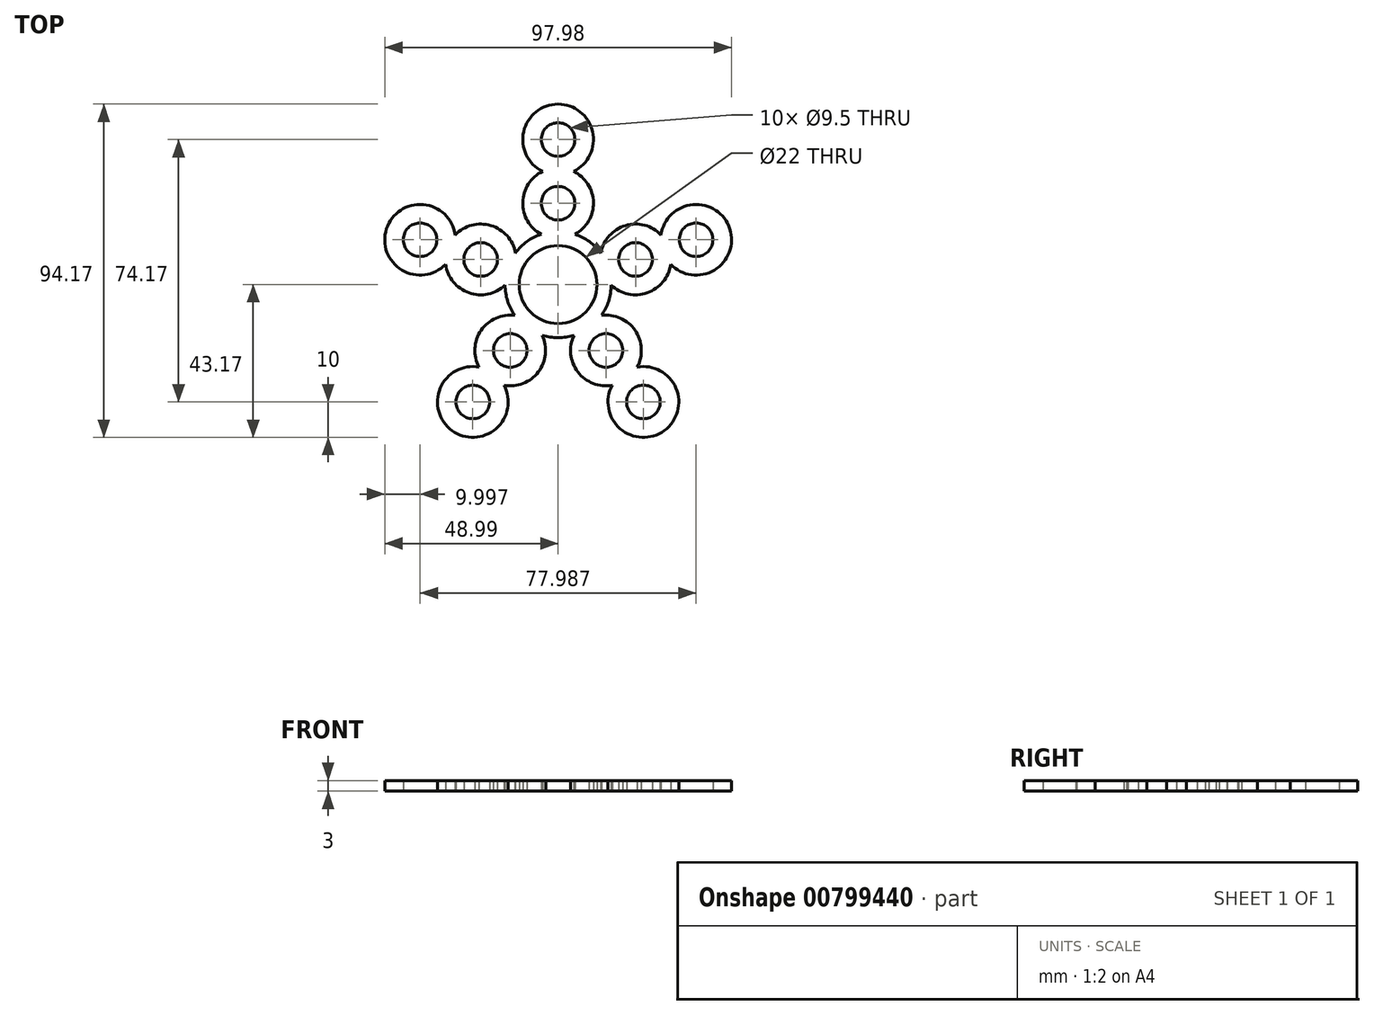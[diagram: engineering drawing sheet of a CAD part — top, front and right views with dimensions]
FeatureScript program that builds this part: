
annotation { "Feature Type Name" : "Feature", "Feature Type Description" : "" }
export const myFeature = defineFeature(function(context is Context, id is Id, definition is map)
    precondition{}
    {
        {
            var Q0;
            Q0=qCreatedBy(makeId("Top.planeOp"),FACE);
            var sketch = newSketch(context, id + "F0", { "sketchPlane" : qUnion([Q0])});
            skCircle(sketch, "E0", {"center": v(0, 0) * mm, "radius": 11 * mm});
            skArc(sketch, "E1", {"start": v(-4.78, 14.22) * mm, "mid": v(-8.82, 12.14) * mm, "end": v(-12.04, 8.94) * mm});
            skLineSegment(sketch, "E2", {"start": v(0, 0) * mm, "end": v(0, 23) * mm});
            skCircle(sketch, "E3", {"center": v(0, 23) * mm, "radius": 4.75 * mm});
            skArc(sketch, "E4", {"start": v(-4.36, 32) * mm, "mid": v(-10, 23.24) * mm, "end": v(-4.78, 14.22) * mm});
            skLineSegment(sketch, "E5", {"start": v(0, 23) * mm, "end": v(0, 41) * mm});
            skCircle(sketch, "E6", {"center": v(0, 41) * mm, "radius": 4.75 * mm});
            skArc(sketch, "E7", {"start": v(4.36, 32) * mm, "mid": v(0, 51) * mm, "end": v(-4.36, 32) * mm});
            skArc(sketch, "E8.trimOffspring", {"start": v(4.78, 14.22) * mm, "mid": v(10, 23.24) * mm, "end": v(4.36, 32) * mm});
            skArc(sketch, "E9.1.0", {"start": v(-29.09, 14.03) * mm, "mid": v(-48.5, 15.76) * mm, "end": v(-31.78, 5.74) * mm});
            skArc(sketch, "E9.1.1", {"start": v(-31.78, 5.74) * mm, "mid": v(-25.19, -2.33) * mm, "end": v(-15, -0.15) * mm});
            skCircle(sketch, "E9.1.2", {"center": v(-21.87, 7.1) * mm, "radius": 4.75 * mm});
            skArc(sketch, "E9.1.3", {"start": v(-12.04, 8.94) * mm, "mid": v(-19.01, 16.69) * mm, "end": v(-29.09, 14.03) * mm});
            skCircle(sketch, "E9.1.4", {"center": v(-39, 12.67) * mm, "radius": 4.75 * mm});
            skArc(sketch, "E9.2.0", {"start": v(-22.34, -23.33) * mm, "mid": v(-29.98, -41.26) * mm, "end": v(-15.28, -28.45) * mm});
            skArc(sketch, "E9.2.1", {"start": v(-15.28, -28.45) * mm, "mid": v(-5.57, -24.68) * mm, "end": v(-4.49, -14.31) * mm});
            skCircle(sketch, "E9.2.2", {"center": v(-13.52, -18.6) * mm, "radius": 4.75 * mm});
            skArc(sketch, "E9.2.3", {"start": v(-12.23, -8.7) * mm, "mid": v(-21.75, -12.92) * mm, "end": v(-22.34, -23.33) * mm});
            skCircle(sketch, "E9.2.4", {"center": v(-24.1, -33.17) * mm, "radius": 4.75 * mm});
            skArc(sketch, "E9.3.0", {"start": v(15.28, -28.45) * mm, "mid": v(29.98, -41.26) * mm, "end": v(22.34, -23.33) * mm});
            skArc(sketch, "E9.3.1", {"start": v(22.34, -23.33) * mm, "mid": v(21.75, -12.92) * mm, "end": v(12.23, -8.7) * mm});
            skCircle(sketch, "E9.3.2", {"center": v(13.52, -18.6) * mm, "radius": 4.75 * mm});
            skArc(sketch, "E9.3.3", {"start": v(4.49, -14.31) * mm, "mid": v(5.57, -24.68) * mm, "end": v(15.28, -28.45) * mm});
            skCircle(sketch, "E9.3.4", {"center": v(24.1, -33.17) * mm, "radius": 4.75 * mm});
            skArc(sketch, "E9.4.0", {"start": v(31.78, 5.74) * mm, "mid": v(48.5, 15.76) * mm, "end": v(29.09, 14.03) * mm});
            skArc(sketch, "E9.4.1", {"start": v(29.09, 14.03) * mm, "mid": v(19.01, 16.69) * mm, "end": v(12.04, 8.94) * mm});
            skCircle(sketch, "E9.4.2", {"center": v(21.87, 7.1) * mm, "radius": 4.75 * mm});
            skArc(sketch, "E9.4.3", {"start": v(15, -0.15) * mm, "mid": v(25.19, -2.33) * mm, "end": v(31.78, 5.74) * mm});
            skCircle(sketch, "E9.4.4", {"center": v(39, 12.67) * mm, "radius": 4.75 * mm});
            skArc(sketch, "E10.trimOffspring", {"start": v(12.04, 8.94) * mm, "mid": v(8.82, 12.14) * mm, "end": v(4.78, 14.22) * mm});
            skArc(sketch, "E11.trimOffspring", {"start": v(-15, -0.15) * mm, "mid": v(-14.27, -4.64) * mm, "end": v(-12.23, -8.7) * mm});
            skArc(sketch, "E12.trimOffspring", {"start": v(-4.49, -14.31) * mm, "mid": v(0, -15) * mm, "end": v(4.49, -14.31) * mm});
            skLineSegment(sketch, "E13.trimOffspring", {"start": v(-26.9, -37.01) * mm, "end": v(-26.92, -37.05) * mm});
            skArc(sketch, "E14.trimOffspring", {"start": v(12.23, -8.7) * mm, "mid": v(14.27, -4.64) * mm, "end": v(15, -0.15) * mm});
            skSolve(sketch);
        }
        {
            var Q0;
            Q0 = qSketchRegion(id + "F0", true);
            extrude(context, id + "F1", {"entities" : qUnion([Q0]), "depth" : 3 * mm, "offsetDistance" : 25 * mm});
        }
    });
